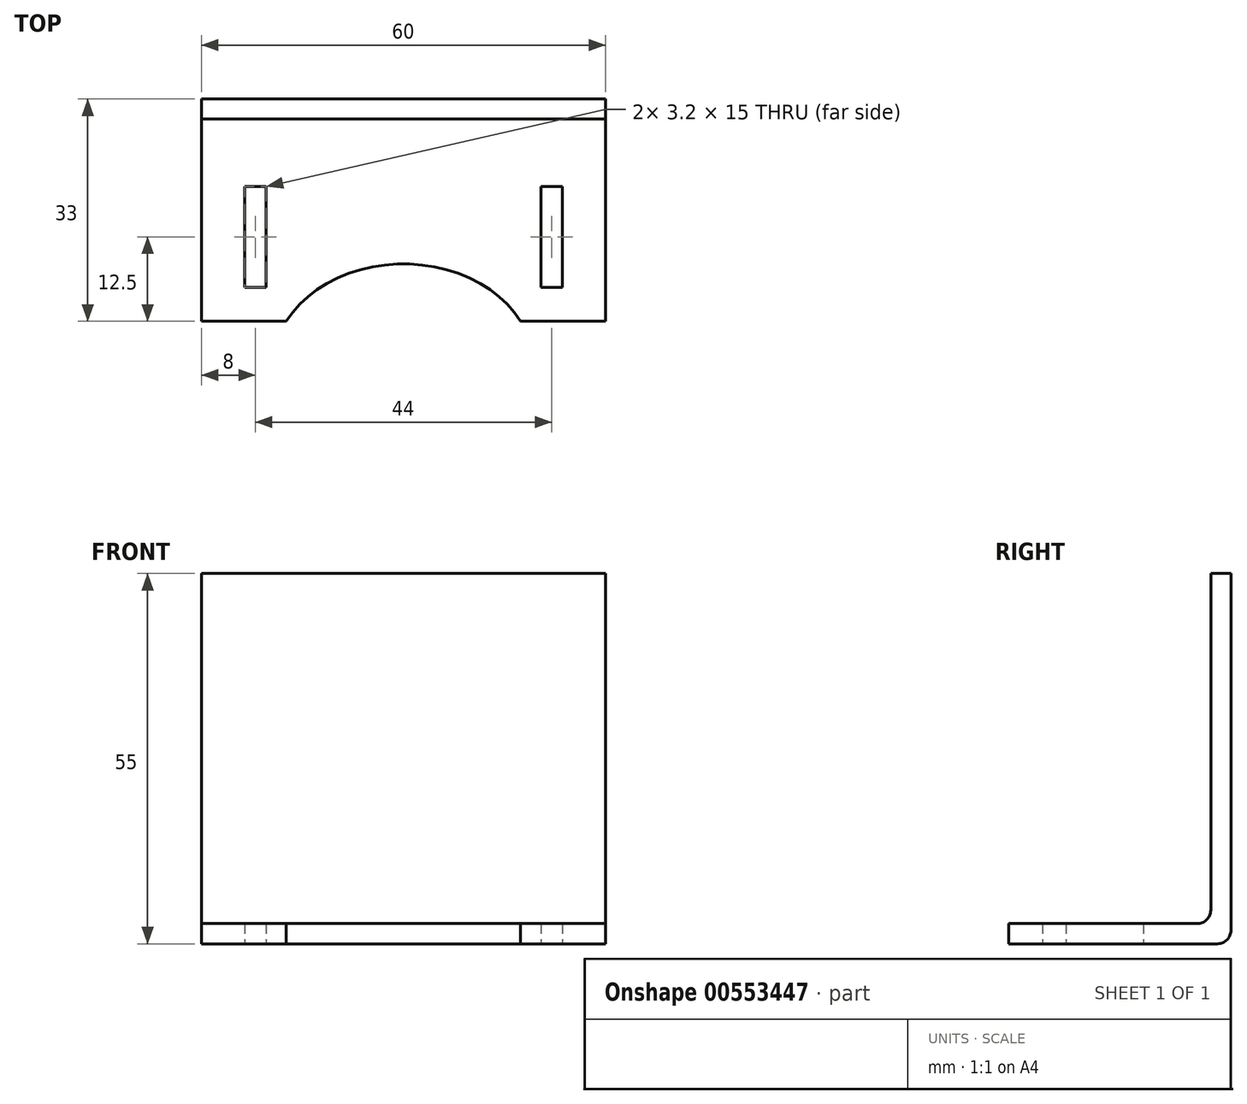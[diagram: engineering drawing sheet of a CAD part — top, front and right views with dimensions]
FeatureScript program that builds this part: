
annotation { "Feature Type Name" : "Feature", "Feature Type Description" : "" }
export const myFeature = defineFeature(function(context is Context, id is Id, definition is map)
    precondition{}
    {
        {
            var Q0;
            Q0=qCreatedBy(makeId("Right.planeOp"),FACE);
            var sketch = newSketch(context, id + "F0", { "sketchPlane" : qUnion([Q0])});
            skLineSegment(sketch, "E0.bottom", {"start": v(-16.5, -27.5) * mm, "end": v(16.5, -27.5) * mm});
            skLineSegment(sketch, "E0.top", {"start": v(-16.5, 27.5) * mm, "end": v(16.5, 27.5) * mm});
            skLineSegment(sketch, "E0.left", {"start": v(-16.5, -27.5) * mm, "end": v(-16.5, 27.5) * mm});
            skLineSegment(sketch, "E0.right", {"start": v(16.5, -27.5) * mm, "end": v(16.5, 27.5) * mm});
            skPoint(sketch, "E0.middle", {"position": v(0, 0) * mm});
            skLineSegment(sketch, "E1.bottom", {"start": v(-16.5, 27.5) * mm, "end": v(13.5, 27.5) * mm});
            skLineSegment(sketch, "E1.top", {"start": v(-16.5, -24.5) * mm, "end": v(13.5, -24.5) * mm});
            skLineSegment(sketch, "E1.left", {"start": v(-16.5, 27.5) * mm, "end": v(-16.5, -24.5) * mm});
            skLineSegment(sketch, "E1.right", {"start": v(13.5, 27.5) * mm, "end": v(13.5, -24.5) * mm});
            skSolve(sketch);
        }
        {
            var Q0;
            Q0=makeQuery(id+"F0.imprint","IMPRINT",FACE,{"disambiguationData":[TD([[makeQuery(id+"F0.imprint","IMPRINT",EDGE,{"derivedFrom":sQuery(id+"F0.wireOp",EDGE,"E0.bottom")}),1.0]])]});
            extrude(context, id + "F1", {"entities" : qUnion([Q0]), "endBound" : BoundingType.SYMMETRIC, "depth" : 60 * mm, "offsetDistance" : 25 * mm, "hasSecondDirection" : true, "secondDirectionOppositeDirection" : true, "secondDirectionDepth" : 25 * mm});
        }
        {
            var Q0;
            Q0=makeQuery(id+"F1.opExtrude","SWEPT_FACE",FACE,{"disambiguationData":[OSD([sQuery(id+"F0.wireOp",EDGE,"E0.bottom")])]});
            var sketch = newSketch(context, id + "F2", { "sketchPlane" : qUnion([Q0])});
            skLineSegment(sketch, "E2.bottom", {"start": v(-23.6, -3.5) * mm, "end": v(-20.4, -3.5) * mm});
            skLineSegment(sketch, "E2.top", {"start": v(-23.6, 11.5) * mm, "end": v(-20.4, 11.5) * mm});
            skLineSegment(sketch, "E2.left", {"start": v(-23.6, -3.5) * mm, "end": v(-23.6, 11.5) * mm});
            skLineSegment(sketch, "E2.right", {"start": v(-20.4, -3.5) * mm, "end": v(-20.4, 11.5) * mm});
            skPoint(sketch, "E2.middle", {"position": v(-22, 4) * mm});
            skLineSegment(sketch, "E3.bottom", {"start": v(20.4, -3.5) * mm, "end": v(23.6, -3.5) * mm});
            skLineSegment(sketch, "E3.top", {"start": v(20.4, 11.5) * mm, "end": v(23.6, 11.5) * mm});
            skLineSegment(sketch, "E3.left", {"start": v(20.4, -3.5) * mm, "end": v(20.4, 11.5) * mm});
            skLineSegment(sketch, "E3.right", {"start": v(23.6, -3.5) * mm, "end": v(23.6, 11.5) * mm});
            skPoint(sketch, "E3.middle", {"position": v(22, 4) * mm});
            skSolve(sketch);
        }
        {
            var Q0;
            Q0=makeQuery(id+"F2.imprint","IMPRINT",FACE,{"disambiguationData":[TD([[makeQuery(id+"F2.imprint","IMPRINT",EDGE,{"derivedFrom":sQuery(id+"F2.wireOp",EDGE,"E3.bottom")}),1.0]])]});
            var Q1;
            Q1=makeQuery(id+"F2.imprint","IMPRINT",FACE,{"disambiguationData":[TD([[makeQuery(id+"F2.imprint","IMPRINT",EDGE,{"derivedFrom":sQuery(id+"F2.wireOp",EDGE,"E2.bottom")}),1.0]])]});
            extrude(context, id + "F3", {"entities" : qUnion([Q0, Q1]), "operationType" : NewBodyOperationType.REMOVE, "oppositeDirection" : true, "depth" : 25 * mm, "offsetDistance" : 25 * mm});
        }
        {
            var Q0;
            Q0=makeQuery(id+"F1.opExtrude","SWEPT_FACE",FACE,{"disambiguationData":[OSD([sQuery(id+"F0.wireOp",EDGE,"E0.bottom")])]});
            var sketch = newSketch(context, id + "F4", { "sketchPlane" : qUnion([Q0])});
            skEllipse(sketch, "E4", {"center": v(0, 23.5) * mm, "majorRadius": 19.5 * mm, "minorRadius": 15.5 * mm, "majorAxis": v(1, 0)});
            skPoint(sketch, "E4.centerSnap0", {"position": v(0, 16.5) * mm});
            skSolve(sketch);
        }
        {
            var Q0;
            Q0 = qSketchRegion(id + "F4", true);
            extrude(context, id + "F5", {"entities" : qUnion([Q0]), "operationType" : NewBodyOperationType.REMOVE, "oppositeDirection" : true, "depth" : 25 * mm, "offsetDistance" : 25 * mm});
        }
        {
            var Q0;
            Q0=makeQuery(id+"F1.opExtrude","SWEPT_EDGE",EDGE,{"disambiguationData":[OSD([sQuery(id+"F0.wireOp",EDGE,"E1.top"),sQuery(id+"F0.wireOp",EDGE,"E1.right")])]});
            var Q1;
            Q1=makeQuery(id+"F1.opExtrude","SWEPT_EDGE",EDGE,{"disambiguationData":[OSD([sQuery(id+"F0.wireOp",EDGE,"E0.bottom"),sQuery(id+"F0.wireOp",EDGE,"E0.right")])]});
            fillet(context, id + "F6", {"entities" : qUnion([Q0, Q1]), "radius" : 2 * mm, "tangentPropagation" : true, "allowEdgeOverflow" : false});
        }
    });
